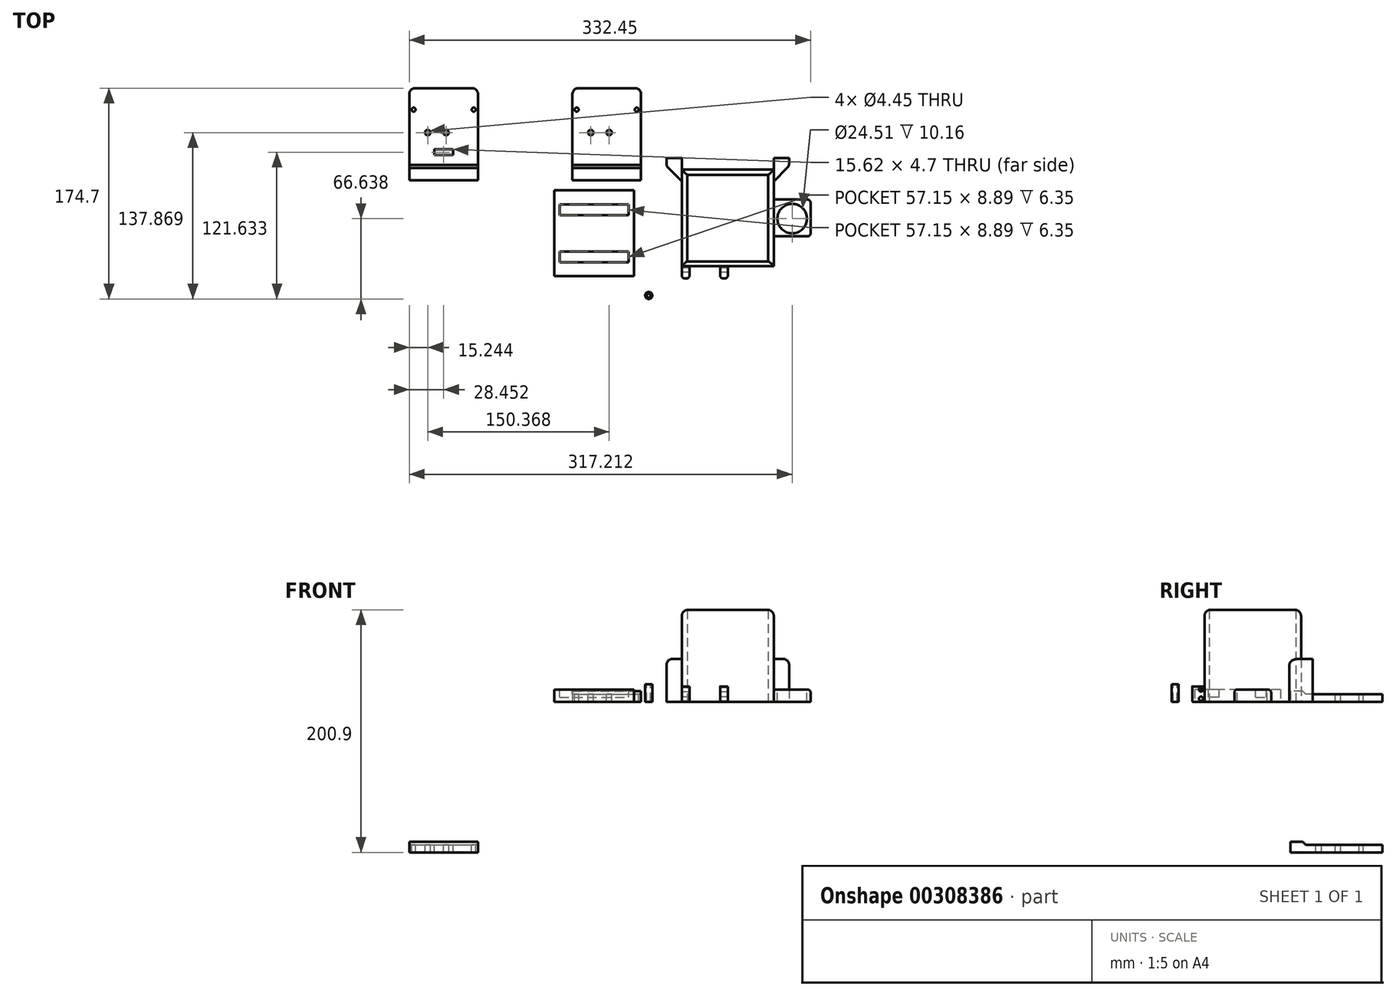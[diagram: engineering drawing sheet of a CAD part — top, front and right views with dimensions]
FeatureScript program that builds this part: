
annotation { "Feature Type Name" : "Feature", "Feature Type Description" : "" }
export const myFeature = defineFeature(function(context is Context, id is Id, definition is map)
    precondition{}
    {
        {
            var Q0;
            Q0=qCreatedBy(makeId("Top.planeOp"),FACE);
            var sketch = newSketch(context, id + "F0", { "sketchPlane" : qUnion([Q0])});
            skLineSegment(sketch, "E0.bottom", {"start": v(-40.77, 32.39) * mm, "end": v(35.43, 32.39) * mm});
            skLineSegment(sketch, "E0.top", {"start": v(-40.77, -43.81) * mm, "end": v(35.43, -43.81) * mm});
            skLineSegment(sketch, "E0.left", {"start": v(-40.77, 32.39) * mm, "end": v(-40.77, -43.81) * mm});
            skLineSegment(sketch, "E0.right", {"start": v(35.43, 32.39) * mm, "end": v(35.43, -43.81) * mm});
            skSolve(sketch);
        }
        {
            var Q0;
            Q0=makeQuery(id+"F0.imprint","IMPRINT",FACE,{"disambiguationData":[TD([[makeQuery(id+"F0.imprint","IMPRINT",EDGE,{"derivedFrom":sQuery(id+"F0.wireOp",EDGE,"E0.bottom")}),-1.0]])]});
            extrude(context, id + "F1", {"entities" : qUnion([Q0]), "depth" : 3.8 * mm});
        }
        {
            var Q0;
            Q0=makeQuery(id+"F1.opExtrude","CAP_FACE",FACE,{"disambiguationData":[OSD([sQuery(id+"F0.wireOp",EDGE,"E0.bottom"),sQuery(id+"F0.wireOp",EDGE,"E0.top"),sQuery(id+"F0.wireOp",EDGE,"E0.left"),sQuery(id+"F0.wireOp",EDGE,"E0.right")])],"isStart":false});
            var sketch = newSketch(context, id + "F2", { "sketchPlane" : qUnion([Q0])});
            skLineSegment(sketch, "E1.bottom", {"start": v(-40.77, -43.81) * mm, "end": v(-34.42, -43.81) * mm});
            skLineSegment(sketch, "E1.top", {"start": v(-40.77, -31.11) * mm, "end": v(-34.42, -31.11) * mm});
            skLineSegment(sketch, "E1.left", {"start": v(-40.77, -43.81) * mm, "end": v(-40.77, -31.11) * mm});
            skLineSegment(sketch, "E1.right", {"start": v(-34.42, -43.81) * mm, "end": v(-34.42, -31.11) * mm});
            skLineSegment(sketch, "E2.bottom", {"start": v(-9.02, -43.81) * mm, "end": v(-2.67, -43.81) * mm});
            skLineSegment(sketch, "E2.top", {"start": v(-9.02, -31.11) * mm, "end": v(-2.67, -31.11) * mm});
            skLineSegment(sketch, "E2.left", {"start": v(-9.02, -43.81) * mm, "end": v(-9.02, -31.11) * mm});
            skLineSegment(sketch, "E2.right", {"start": v(-2.67, -43.81) * mm, "end": v(-2.67, -31.11) * mm});
            skSolve(sketch);
        }
        {
            var Q0;
            Q0 = qSketchRegion(id + "F2", true);
            extrude(context, id + "F3", {"entities" : qUnion([Q0]), "operationType" : NewBodyOperationType.ADD, "depth" : 10.16 * mm});
        }
        {
            var Q0;
            Q0=makeQuery(id+"F3.opExtrude","SWEPT_FACE",FACE,{"disambiguationData":[OSD([sQuery(id+"F2.wireOp",EDGE,"E2.right")])]});
            var sketch = newSketch(context, id + "F4", { "sketchPlane" : qUnion([Q0])});
            skCircle(sketch, "E3", {"center": v(-41.27, 6.65) * mm, "radius": 1.71 * mm});
            skCircle(sketch, "E4", {"center": v(-33.65, 6.65) * mm, "radius": 1.71 * mm});
            skSolve(sketch);
        }
        {
            var Q0;
            Q0 = qSketchRegion(id + "F4", true);
            extrude(context, id + "F5", {"entities" : qUnion([Q0]), "operationType" : NewBodyOperationType.REMOVE, "oppositeDirection" : true, "depth" : 50.8 * mm});
        }
        {
            var Q0;
            Q0=makeQuery(id+"F1.opExtrude","SWEPT_BODY",BODY,{"disambiguationData":[OSD([sQuery(id+"F0.wireOp",EDGE,"E0.bottom"),sQuery(id+"F0.wireOp",EDGE,"E0.top"),sQuery(id+"F0.wireOp",EDGE,"E0.left"),sQuery(id+"F0.wireOp",EDGE,"E0.right")])]});
            var Q1;
            Q1=makeQuery(id+"F1.opExtrude","CAP_EDGE",EDGE,{"disambiguationData":[OSD([sQuery(id+"F0.wireOp",EDGE,"E0.top")])],"isStart":true});
            transform(context, id + "F6", {"entities" : qUnion([Q0]), "transformType" : TransformType.ROTATION, "transformAxis" : qUnion([Q1]), "angle" : 90 * degree, "makeCopy" : false});
        }
        {
            var Q0;
            Q0=makeQuery(id+"F1.opExtrude","CAP_FACE",FACE,{"disambiguationData":[OSD([sQuery(id+"F0.wireOp",EDGE,"E0.bottom"),sQuery(id+"F0.wireOp",EDGE,"E0.top"),sQuery(id+"F0.wireOp",EDGE,"E0.left"),sQuery(id+"F0.wireOp",EDGE,"E0.right")])],"isStart":true});
            var sketch = newSketch(context, id + "F7", { "sketchPlane" : qUnion([Q0])});
            skLineSegment(sketch, "E5.bottom", {"start": v(40.77, 76.2) * mm, "end": v(36.32, 76.2) * mm});
            skLineSegment(sketch, "E5.top", {"start": v(40.77, 0) * mm, "end": v(36.32, 0) * mm});
            skLineSegment(sketch, "E5.left", {"start": v(40.77, 76.2) * mm, "end": v(40.77, 0) * mm});
            skLineSegment(sketch, "E5.right", {"start": v(36.32, 76.2) * mm, "end": v(36.32, 0) * mm});
            skSolve(sketch);
        }
        {
            var Q0;
            Q0=makeQuery(id+"F7.imprint","IMPRINT",FACE,{"disambiguationData":[TD([[makeQuery(id+"F7.imprint","IMPRINT",EDGE,{"derivedFrom":sQuery(id+"F7.wireOp",EDGE,"E5.bottom")}),1.0]])]});
            extrude(context, id + "F8", {"entities" : qUnion([Q0]), "operationType" : NewBodyOperationType.ADD, "depth" : 76.2 * mm});
        }
        {
            var Q0;
            Q0=makeQuery(id+"F8.opExtrude","SWEPT_FACE",FACE,{"disambiguationData":[OSD([sQuery(id+"F7.wireOp",EDGE,"E5.right")])]});
            var sketch = newSketch(context, id + "F9", { "sketchPlane" : qUnion([Q0])});
            skLineSegment(sketch, "E6.bottom", {"start": v(32.39, 76.2) * mm, "end": v(27.94, 76.2) * mm});
            skLineSegment(sketch, "E6.top", {"start": v(32.39, 0) * mm, "end": v(27.94, 0) * mm});
            skLineSegment(sketch, "E6.left", {"start": v(32.39, 76.2) * mm, "end": v(32.39, 0) * mm});
            skLineSegment(sketch, "E6.right", {"start": v(27.94, 76.2) * mm, "end": v(27.94, 0) * mm});
            skSolve(sketch);
        }
        {
            var Q0;
            Q0=makeQuery(id+"F9.imprint","IMPRINT",FACE,{"disambiguationData":[TD([[makeQuery(id+"F9.imprint","IMPRINT",EDGE,{"derivedFrom":sQuery(id+"F9.wireOp",EDGE,"E6.bottom")}),1.0]])]});
            extrude(context, id + "F10", {"entities" : qUnion([Q0]), "operationType" : NewBodyOperationType.ADD, "depth" : 71.75 * mm});
        }
        {
            var Q0;
            Q0=makeQuery(id+"F10.opExtrude","SWEPT_FACE",FACE,{"disambiguationData":[OSD([sQuery(id+"F9.wireOp",EDGE,"E6.right")])]});
            var sketch = newSketch(context, id + "F11", { "sketchPlane" : qUnion([Q0])});
            skLineSegment(sketch, "E7.bottom", {"start": v(35.43, 76.2) * mm, "end": v(30.72, 76.2) * mm});
            skLineSegment(sketch, "E7.top", {"start": v(35.43, 0) * mm, "end": v(30.72, 0) * mm});
            skLineSegment(sketch, "E7.left", {"start": v(35.43, 76.2) * mm, "end": v(35.43, 0) * mm});
            skLineSegment(sketch, "E7.right", {"start": v(30.72, 76.2) * mm, "end": v(30.72, 0) * mm});
            skSolve(sketch);
        }
        {
            var Q0;
            Q0=makeQuery(id+"F11.imprint","IMPRINT",FACE,{"disambiguationData":[TD([[makeQuery(id+"F11.imprint","IMPRINT",EDGE,{"derivedFrom":sQuery(id+"F11.wireOp",EDGE,"E7.bottom")}),1.0]])]});
            extrude(context, id + "F12", {"entities" : qUnion([Q0]), "operationType" : NewBodyOperationType.ADD, "depth" : 73.53 * mm});
        }
        {
            var Q0;
            Q0=makeQuery(id+"F12.boolean.opBoolean","MERGE",FACE,{"derivedFrom":[makeQuery(id+"F10.opExtrude","CAP_FACE",FACE,{"disambiguationData":[OSD([sQuery(id+"F9.wireOp",EDGE,"E6.bottom"),sQuery(id+"F9.wireOp",EDGE,"E6.top"),sQuery(id+"F9.wireOp",EDGE,"E6.left"),sQuery(id+"F9.wireOp",EDGE,"E6.right")])],"isStart":false}),makeQuery(id+"F12.opExtrude","SWEPT_FACE",FACE,{"disambiguationData":[OSD([sQuery(id+"F11.wireOp",EDGE,"E7.left")])]})]});
            var sketch = newSketch(context, id + "F13", { "sketchPlane" : qUnion([Q0])});
            skSolve(sketch);
        }
        {
            var Q0;
            Q0=makeQuery(id+"F8.boolean.opBoolean","MERGE",EDGE,{"derivedFrom":[makeQuery(id+"F1.opExtrude","SWEPT_EDGE",EDGE,{"disambiguationData":[OSD([sQuery(id+"F0.wireOp",EDGE,"E0.bottom"),sQuery(id+"F0.wireOp",EDGE,"E0.left")])]}),makeQuery(id+"F8.opExtrude","SWEPT_EDGE",EDGE,{"disambiguationData":[OSD([sQuery(id+"F7.wireOp",EDGE,"E5.bottom"),sQuery(id+"F7.wireOp",EDGE,"E5.left")])]})]});
            var Q1;
            Q1=makeQuery(id+"F1.opExtrude","CAP_EDGE",EDGE,{"disambiguationData":[OSD([sQuery(id+"F0.wireOp",EDGE,"E0.bottom")])],"isStart":false});
            var Q2;
            Q2=makeQuery(id+"F12.boolean.opBoolean","MERGE",EDGE,{"derivedFrom":[makeQuery(id+"F1.opExtrude","SWEPT_EDGE",EDGE,{"disambiguationData":[OSD([sQuery(id+"F0.wireOp",EDGE,"E0.bottom"),sQuery(id+"F0.wireOp",EDGE,"E0.right")])]}),makeQuery(id+"F10.opExtrude","CAP_EDGE",EDGE,{"disambiguationData":[OSD([sQuery(id+"F9.wireOp",EDGE,"E6.bottom")])],"isStart":false}),makeQuery(id+"F12.opExtrude","SWEPT_EDGE",EDGE,{"disambiguationData":[OSD([sQuery(id+"F11.wireOp",EDGE,"E7.bottom"),sQuery(id+"F11.wireOp",EDGE,"E7.left")])]})]});
            var Q3;
            Q3=makeQuery(id+"F10.boolean.opBoolean","MERGE",EDGE,{"derivedFrom":[makeQuery(id+"F8.opExtrude","CAP_EDGE",EDGE,{"disambiguationData":[OSD([sQuery(id+"F7.wireOp",EDGE,"E5.bottom")])],"isStart":false}),makeQuery(id+"F10.opExtrude","SWEPT_EDGE",EDGE,{"disambiguationData":[OSD([sQuery(id+"F9.wireOp",EDGE,"E6.bottom"),sQuery(id+"F9.wireOp",EDGE,"E6.left")])]})]});
            fillet(context, id + "F14", {"entities" : qUnion([Q0, Q1, Q2, Q3]), "radius" : 5.08 * mm, "tangentPropagation" : true, "allowEdgeOverflow" : false});
        }
        {
            var Q0;
            Q0=makeQuery(id+"F10.boolean.opBoolean","MERGE",FACE,{"derivedFrom":[makeQuery(id+"F8.opExtrude","CAP_FACE",FACE,{"disambiguationData":[OSD([sQuery(id+"F7.wireOp",EDGE,"E5.bottom"),sQuery(id+"F7.wireOp",EDGE,"E5.top"),sQuery(id+"F7.wireOp",EDGE,"E5.left"),sQuery(id+"F7.wireOp",EDGE,"E5.right")])],"isStart":false}),makeQuery(id+"F10.opExtrude","SWEPT_FACE",FACE,{"disambiguationData":[OSD([sQuery(id+"F9.wireOp",EDGE,"E6.left")])]})]});
            var sketch = newSketch(context, id + "F15", { "sketchPlane" : qUnion([Q0])});
            skLineSegment(sketch, "E8.bottom", {"start": v(-35.43, 0) * mm, "end": v(-48.13, 0) * mm});
            skLineSegment(sketch, "E8.top", {"start": v(-35.43, 35.56) * mm, "end": v(-48.13, 35.56) * mm});
            skLineSegment(sketch, "E8.left", {"start": v(-35.43, 0) * mm, "end": v(-35.43, 35.56) * mm});
            skLineSegment(sketch, "E8.right", {"start": v(-48.13, 0) * mm, "end": v(-48.13, 35.56) * mm});
            skLineSegment(sketch, "E9.bottom", {"start": v(40.77, 0) * mm, "end": v(53.47, 0) * mm});
            skLineSegment(sketch, "E9.top", {"start": v(40.77, 35.56) * mm, "end": v(53.47, 35.56) * mm});
            skLineSegment(sketch, "E9.left", {"start": v(40.77, 0) * mm, "end": v(40.77, 35.56) * mm});
            skLineSegment(sketch, "E9.right", {"start": v(53.47, 0) * mm, "end": v(53.47, 35.56) * mm});
            skSolve(sketch);
        }
        {
            var Q0;
            Q0=makeQuery(id+"F15.imprint","IMPRINT",FACE,{"disambiguationData":[TD([[makeQuery(id+"F15.imprint","IMPRINT",EDGE,{"derivedFrom":sQuery(id+"F15.wireOp",EDGE,"E8.bottom")}),-1.0]])]});
            var Q1;
            Q1=makeQuery(id+"F15.imprint","IMPRINT",FACE,{"disambiguationData":[TD([[makeQuery(id+"F15.imprint","IMPRINT",EDGE,{"derivedFrom":sQuery(id+"F15.wireOp",EDGE,"E9.bottom")}),1.0]])]});
            extrude(context, id + "F16", {"entities" : qUnion([Q0, Q1]), "operationType" : NewBodyOperationType.ADD, "endBound" : BoundingType.SYMMETRIC, "depth" : 19.3 * mm});
        }
        {
            var Q0;
            Q0=makeQuery(id+"F16.opExtrude","CAP_EDGE",EDGE,{"disambiguationData":[OSD([sQuery(id+"F15.wireOp",EDGE,"E8.right")])],"isStart":true});
            var Q1;
            Q1=makeQuery(id+"F16.opExtrude","CAP_EDGE",EDGE,{"disambiguationData":[OSD([sQuery(id+"F15.wireOp",EDGE,"E9.right")])],"isStart":true});
            chamfer(context, id + "F17", {"entities" : qUnion([Q0, Q1]), "width" : 12.7 * mm, "tangentPropagation" : true});
        }
        {
            var Q0;
            Q0=makeQuery(id+"F16.opExtrude","SWEPT_EDGE",EDGE,{"disambiguationData":[OSD([sQuery(id+"F15.wireOp",EDGE,"E9.top"),sQuery(id+"F15.wireOp",EDGE,"E9.right")])]});
            var Q1;
            Q1=makeQuery(id+"F16.opExtrude","SWEPT_EDGE",EDGE,{"disambiguationData":[OSD([sQuery(id+"F15.wireOp",EDGE,"E8.top"),sQuery(id+"F15.wireOp",EDGE,"E8.right")])]});
            var Q2;
            Q2=makeQuery(id+"F17.opChamfer","BLEND_EDGE",EDGE,{"blendedFrom":[makeQuery(id+"F16.opExtrude","CAP_EDGE",EDGE,{"disambiguationData":[OSD([sQuery(id+"F15.wireOp",EDGE,"E9.right")])],"isStart":true}),makeQuery(id+"F16.opExtrude","SWEPT_FACE",FACE,{"disambiguationData":[OSD([sQuery(id+"F15.wireOp",EDGE,"E9.top")])]})],"blendedInto":[makeQuery(id+"F16.opExtrude","SWEPT_FACE",FACE,{"disambiguationData":[OSD([sQuery(id+"F15.wireOp",EDGE,"E9.top")])]})]});
            var Q3;
            {var subQ0=sQuery(id+"F15.wireOp",EDGE,"E9.right");Q3=makeQuery(id+"F17.opChamfer","BLEND_EDGE",EDGE,{"blendedFrom":[makeQuery(id+"F16.opExtrude","CAP_EDGE",EDGE,{"disambiguationData":[OSD([subQ0])],"isStart":true}),makeQuery(id+"F16.opExtrude","SWEPT_FACE",FACE,{"disambiguationData":[OSD([subQ0])]})],"blendedInto":[makeQuery(id+"F16.opExtrude","SWEPT_FACE",FACE,{"disambiguationData":[OSD([subQ0])]})]});}
            var Q4;
            Q4=makeQuery(id+"F17.opChamfer","BLEND_EDGE",EDGE,{"blendedFrom":[makeQuery(id+"F16.opExtrude","CAP_EDGE",EDGE,{"disambiguationData":[OSD([sQuery(id+"F15.wireOp",EDGE,"E8.right")])],"isStart":true}),makeQuery(id+"F16.opExtrude","SWEPT_FACE",FACE,{"disambiguationData":[OSD([sQuery(id+"F15.wireOp",EDGE,"E8.top")])]})],"blendedInto":[makeQuery(id+"F16.opExtrude","SWEPT_FACE",FACE,{"disambiguationData":[OSD([sQuery(id+"F15.wireOp",EDGE,"E8.top")])]})]});
            var Q5;
            {var subQ0=sQuery(id+"F15.wireOp",EDGE,"E8.right");Q5=makeQuery(id+"F17.opChamfer","BLEND_EDGE",EDGE,{"blendedFrom":[makeQuery(id+"F16.opExtrude","CAP_EDGE",EDGE,{"disambiguationData":[OSD([subQ0])],"isStart":true}),makeQuery(id+"F16.opExtrude","SWEPT_FACE",FACE,{"disambiguationData":[OSD([subQ0])]})],"blendedInto":[makeQuery(id+"F16.opExtrude","SWEPT_FACE",FACE,{"disambiguationData":[OSD([subQ0])]})]});}
            fillet(context, id + "F18", {"entities" : qUnion([Q0, Q1, Q2, Q3, Q4, Q5]), "radius" : 5.08 * mm, "tangentPropagation" : true, "allowEdgeOverflow" : false});
        }
        {
            var Q0;
            {var subQ0=sQuery(id+"F0.wireOp",EDGE,"E0.right");Q0=makeQuery(id+"F13.imprint","IMPRINT",FACE,{"disambiguationData":[TD([[makeQuery(id+"F13.imprint","IMPRINT",EDGE,{"derivedFrom":makeQuery(id+"F1.opExtrude","CAP_EDGE",EDGE,{"disambiguationData":[OSD([subQ0])],"isStart":false})}),1.0]])]});}
            var sketch = newSketch(context, id + "F19", { "sketchPlane" : qUnion([Q0])});
            skLineSegment(sketch, "E10.bottom", {"start": v(-22.86, 0) * mm, "end": v(7.62, 0) * mm});
            skLineSegment(sketch, "E10.top", {"start": v(-22.86, 10.16) * mm, "end": v(7.62, 10.16) * mm});
            skLineSegment(sketch, "E10.left", {"start": v(-22.86, 0) * mm, "end": v(-22.86, 10.16) * mm});
            skLineSegment(sketch, "E10.right", {"start": v(7.62, 0) * mm, "end": v(7.62, 10.16) * mm});
            skSolve(sketch);
        }
        {
            var Q0;
            Q0 = qSketchRegion(id + "F19", true);
            extrude(context, id + "F20", {"entities" : qUnion([Q0]), "operationType" : NewBodyOperationType.ADD, "depth" : 30.48 * mm});
        }
        {
            var Q0;
            Q0=makeQuery(id+"F20.opExtrude","SWEPT_FACE",FACE,{"disambiguationData":[OSD([sQuery(id+"F19.wireOp",EDGE,"E10.top")])]});
            var sketch = newSketch(context, id + "F21", { "sketchPlane" : qUnion([Q0])});
            skCircle(sketch, "E11", {"center": v(50.67, -8.11) * mm, "radius": 12.26 * mm});
            skSolve(sketch);
        }
        {
            var Q0;
            Q0=makeQuery(id+"F21.imprint","IMPRINT",FACE,{"disambiguationData":[TD([[makeQuery(id+"F21.imprint","IMPRINT",EDGE,{"derivedFrom":sQuery(id+"F21.wireOp",EDGE,"E11")}),1.0]])]});
            extrude(context, id + "F22", {"entities" : qUnion([Q0]), "operationType" : NewBodyOperationType.REMOVE, "oppositeDirection" : true, "depth" : 25.4 * mm});
        }
        {
            var Q0;
            Q0=makeQuery(id+"F20.opExtrude","SWEPT_EDGE",EDGE,{"disambiguationData":[OSD([sQuery(id+"F19.wireOp",EDGE,"E10.top"),sQuery(id+"F19.wireOp",EDGE,"E10.left")])]});
            var Q1;
            Q1=makeQuery(id+"F20.opExtrude","CAP_EDGE",EDGE,{"disambiguationData":[OSD([sQuery(id+"F19.wireOp",EDGE,"E10.top")])],"isStart":false});
            var Q2;
            Q2=makeQuery(id+"F20.opExtrude","SWEPT_EDGE",EDGE,{"disambiguationData":[OSD([sQuery(id+"F19.wireOp",EDGE,"E10.top"),sQuery(id+"F19.wireOp",EDGE,"E10.right")])]});
            var Q3;
            Q3=makeQuery(id+"F20.opExtrude","CAP_EDGE",EDGE,{"disambiguationData":[OSD([sQuery(id+"F19.wireOp",EDGE,"E10.left")])],"isStart":false});
            var Q4;
            Q4=makeQuery(id+"F20.opExtrude","CAP_EDGE",EDGE,{"disambiguationData":[OSD([sQuery(id+"F19.wireOp",EDGE,"E10.right")])],"isStart":false});
            var Q5;
            Q5=makeQuery(id+"F20.opExtrude","CAP_EDGE",EDGE,{"disambiguationData":[OSD([sQuery(id+"F19.wireOp",EDGE,"E10.left")])],"isStart":true});
            fillet(context, id + "F23", {"entities" : qUnion([Q0, Q1, Q2, Q3, Q4, Q5]), "radius" : 2.54 * mm, "tangentPropagation" : true, "allowEdgeOverflow" : false});
        }
        {
            var Q0;
            Q0=makeQuery(id+"F3.opExtrude","CAP_EDGE",EDGE,{"disambiguationData":[OSD([sQuery(id+"F2.wireOp",EDGE,"E2.top")])],"isStart":true});
            var Q1;
            Q1=makeQuery(id+"F3.opExtrude","CAP_EDGE",EDGE,{"disambiguationData":[OSD([sQuery(id+"F2.wireOp",EDGE,"E1.top")])],"isStart":true});
            var Q2;
            Q2=makeQuery(id+"F3.opExtrude","CAP_EDGE",EDGE,{"disambiguationData":[OSD([sQuery(id+"F2.wireOp",EDGE,"E1.right")])],"isStart":false});
            var Q3;
            Q3=makeQuery(id+"F3.opExtrude","CAP_EDGE",EDGE,{"disambiguationData":[OSD([sQuery(id+"F2.wireOp",EDGE,"E1.left")])],"isStart":false});
            var Q4;
            Q4=makeQuery(id+"F3.opExtrude","CAP_EDGE",EDGE,{"disambiguationData":[OSD([sQuery(id+"F2.wireOp",EDGE,"E2.left")])],"isStart":false});
            var Q5;
            Q5=makeQuery(id+"F3.opExtrude","CAP_EDGE",EDGE,{"disambiguationData":[OSD([sQuery(id+"F2.wireOp",EDGE,"E2.right")])],"isStart":false});
            fillet(context, id + "F24", {"entities" : qUnion([Q0, Q1, Q2, Q3, Q4, Q5]), "radius" : 2.54 * mm, "tangentPropagation" : true, "allowEdgeOverflow" : false});
        }
        {
            var Q0;
            Q0=qCreatedBy(makeId("Top.planeOp"),FACE);
            var sketch = newSketch(context, id + "F25", { "sketchPlane" : qUnion([Q0])});
            skLineSegment(sketch, "E12.bottom", {"start": v(-146.35, 15.3) * mm, "end": v(-80.31, 15.3) * mm});
            skLineSegment(sketch, "E12.top", {"start": v(-146.35, -55.82) * mm, "end": v(-80.31, -55.82) * mm});
            skLineSegment(sketch, "E12.left", {"start": v(-146.35, 15.3) * mm, "end": v(-146.35, -55.82) * mm});
            skLineSegment(sketch, "E12.right", {"start": v(-80.31, 15.3) * mm, "end": v(-80.31, -55.82) * mm});
            skSolve(sketch);
        }
        {
            var Q0;
            Q0=makeQuery(id+"F25.imprint","IMPRINT",FACE,{"disambiguationData":[TD([[makeQuery(id+"F25.imprint","IMPRINT",EDGE,{"derivedFrom":sQuery(id+"F25.wireOp",EDGE,"E12.bottom")}),-1.0]])]});
            extrude(context, id + "F26", {"entities" : qUnion([Q0]), "depth" : 10.16 * mm});
        }
        {
            var Q0;
            Q0=makeQuery(id+"F26.opExtrude","CAP_FACE",FACE,{"disambiguationData":[OSD([sQuery(id+"F25.wireOp",EDGE,"E12.bottom"),sQuery(id+"F25.wireOp",EDGE,"E12.top"),sQuery(id+"F25.wireOp",EDGE,"E12.left"),sQuery(id+"F25.wireOp",EDGE,"E12.right")])],"isStart":false});
            var sketch = newSketch(context, id + "F27", { "sketchPlane" : qUnion([Q0])});
            skLineSegment(sketch, "E13.bottom", {"start": v(-141.9, -5.15) * mm, "end": v(-84.76, -5.15) * mm});
            skLineSegment(sketch, "E13.top", {"start": v(-141.9, 3.74) * mm, "end": v(-84.76, 3.74) * mm});
            skLineSegment(sketch, "E13.left", {"start": v(-141.9, -5.15) * mm, "end": v(-141.9, 3.74) * mm});
            skLineSegment(sketch, "E13.right", {"start": v(-84.76, -5.15) * mm, "end": v(-84.76, 3.74) * mm});
            skLineSegment(sketch, "E14.bottom", {"start": v(-141.9, -35.37) * mm, "end": v(-84.76, -35.37) * mm});
            skLineSegment(sketch, "E14.top", {"start": v(-141.9, -44.26) * mm, "end": v(-84.76, -44.26) * mm});
            skLineSegment(sketch, "E14.left", {"start": v(-141.9, -35.37) * mm, "end": v(-141.9, -44.26) * mm});
            skLineSegment(sketch, "E14.right", {"start": v(-84.76, -35.37) * mm, "end": v(-84.76, -44.26) * mm});
            skSolve(sketch);
        }
        {
            var Q0;
            Q0 = qSketchRegion(id + "F27", true);
            extrude(context, id + "F28", {"entities" : qUnion([Q0]), "operationType" : NewBodyOperationType.REMOVE, "oppositeDirection" : true, "depth" : 6.35 * mm});
        }
        {
            var Q0;
            Q0=qCreatedBy(makeId("Top.planeOp"),FACE);
            var sketch = newSketch(context, id + "F29", { "sketchPlane" : qUnion([Q0])});
            skCircle(sketch, "E15", {"center": v(-68.17, -71.83) * mm, "radius": 2.92 * mm});
            skSolve(sketch);
        }
        {
            var Q0;
            Q0=makeQuery(id+"F29.imprint","IMPRINT",FACE,{"disambiguationData":[TD([[makeQuery(id+"F29.imprint","IMPRINT",EDGE,{"derivedFrom":sQuery(id+"F29.wireOp",EDGE,"E15")}),1.0]])]});
            extrude(context, id + "F30", {"entities" : qUnion([Q0]), "depth" : 14.6 * mm});
        }
        {
            var Q0;
            Q0=makeQuery(id+"F30.opExtrude","CAP_FACE",FACE,{"disambiguationData":[OSD([sQuery(id+"F29.wireOp",EDGE,"E15")])],"isStart":false});
            var sketch = newSketch(context, id + "F31", { "sketchPlane" : qUnion([Q0])});
            skCircle(sketch, "E16", {"center": v(-68.17, -71.83) * mm, "radius": 1.59 * mm});
            skSolve(sketch);
        }
        {
            var Q0;
            Q0=makeQuery(id+"F31.imprint","IMPRINT",FACE,{"disambiguationData":[TD([[makeQuery(id+"F31.imprint","IMPRINT",EDGE,{"derivedFrom":sQuery(id+"F31.wireOp",EDGE,"E16")}),1.0]])]});
            extrude(context, id + "F32", {"entities" : qUnion([Q0]), "operationType" : NewBodyOperationType.REMOVE, "oppositeDirection" : true, "depth" : 25.4 * mm});
        }
        {
            var Q0;
            Q0=qCreatedBy(makeId("Top.planeOp"),FACE);
            var sketch = newSketch(context, id + "F33", { "sketchPlane" : qUnion([Q0])});
            skLineSegment(sketch, "E17.bottom", {"start": v(-131.4, 99.95) * mm, "end": v(-74.51, 99.95) * mm});
            skLineSegment(sketch, "E17.top", {"start": v(-131.4, 23.75) * mm, "end": v(-74.51, 23.75) * mm});
            skLineSegment(sketch, "E17.left", {"start": v(-131.4, 99.95) * mm, "end": v(-131.4, 23.75) * mm});
            skLineSegment(sketch, "E17.right", {"start": v(-74.51, 99.95) * mm, "end": v(-74.51, 23.75) * mm});
            skSolve(sketch);
        }
        {
            var Q0;
            Q0=makeQuery(id+"F33.imprint","IMPRINT",FACE,{"disambiguationData":[TD([[makeQuery(id+"F33.imprint","IMPRINT",EDGE,{"derivedFrom":sQuery(id+"F33.wireOp",EDGE,"E17.bottom")}),-1.0]])]});
            extrude(context, id + "F34", {"entities" : qUnion([Q0]), "depth" : 6.35 * mm});
        }
        {
            var Q0;
            Q0=makeQuery(id+"F34.opExtrude","SWEPT_EDGE",EDGE,{"disambiguationData":[OSD([sQuery(id+"F33.wireOp",EDGE,"E17.bottom"),sQuery(id+"F33.wireOp",EDGE,"E17.left")])]});
            var Q1;
            Q1=makeQuery(id+"F34.opExtrude","SWEPT_EDGE",EDGE,{"disambiguationData":[OSD([sQuery(id+"F33.wireOp",EDGE,"E17.bottom"),sQuery(id+"F33.wireOp",EDGE,"E17.right")])]});
            fillet(context, id + "F35", {"entities" : qUnion([Q0, Q1]), "radius" : 5.08 * mm, "tangentPropagation" : true, "allowEdgeOverflow" : false});
        }
        {
            var Q0;
            Q0=makeQuery(id+"F34.opExtrude","CAP_FACE",FACE,{"disambiguationData":[OSD([sQuery(id+"F33.wireOp",EDGE,"E17.bottom"),sQuery(id+"F33.wireOp",EDGE,"E17.top"),sQuery(id+"F33.wireOp",EDGE,"E17.left"),sQuery(id+"F33.wireOp",EDGE,"E17.right")])],"isStart":false});
            var sketch = newSketch(context, id + "F36", { "sketchPlane" : qUnion([Q0])});
            skLineSegment(sketch, "E18.bottom", {"start": v(-131.4, 23.75) * mm, "end": v(-74.51, 23.75) * mm});
            skLineSegment(sketch, "E18.top", {"start": v(-131.4, 36.45) * mm, "end": v(-74.51, 36.45) * mm});
            skLineSegment(sketch, "E18.left", {"start": v(-131.4, 23.75) * mm, "end": v(-131.4, 36.45) * mm});
            skLineSegment(sketch, "E18.right", {"start": v(-74.51, 23.75) * mm, "end": v(-74.51, 36.45) * mm});
            skSolve(sketch);
        }
        {
            var Q0;
            Q0=makeQuery(id+"F36.imprint","IMPRINT",FACE,{"disambiguationData":[TD([[makeQuery(id+"F36.imprint","IMPRINT",EDGE,{"derivedFrom":sQuery(id+"F36.wireOp",EDGE,"E18.bottom")}),1.0]])]});
            extrude(context, id + "F37", {"entities" : qUnion([Q0]), "operationType" : NewBodyOperationType.ADD, "depth" : 2.54 * mm});
        }
        {
            var Q0;
            Q0=makeQuery(id+"F37.opExtrude","CAP_EDGE",EDGE,{"disambiguationData":[OSD([sQuery(id+"F36.wireOp",EDGE,"E18.top")])],"isStart":false});
            chamfer(context, id + "F38", {"entities" : qUnion([Q0]), "width" : 2.54 * mm, "tangentPropagation" : true});
        }
        {
            var Q0;
            Q0=makeQuery(id+"F34.opExtrude","CAP_FACE",FACE,{"disambiguationData":[OSD([sQuery(id+"F33.wireOp",EDGE,"E17.bottom"),sQuery(id+"F33.wireOp",EDGE,"E17.top"),sQuery(id+"F33.wireOp",EDGE,"E17.left"),sQuery(id+"F33.wireOp",EDGE,"E17.right")])],"isStart":false});
            var sketch = newSketch(context, id + "F39", { "sketchPlane" : qUnion([Q0])});
            skCircle(sketch, "E19", {"center": v(-78.07, 82.17) * mm, "radius": 1.65 * mm});
            skCircle(sketch, "E20", {"center": v(-127.85, 82.17) * mm, "radius": 1.65 * mm});
            skCircle(sketch, "E21", {"center": v(-100.93, 63.12) * mm, "radius": 2.22 * mm});
            skCircle(sketch, "E22", {"center": v(-116.17, 63.12) * mm, "radius": 2.22 * mm});
            skSolve(sketch);
        }
        {
            var Q0;
            Q0 = qSketchRegion(id + "F39", true);
            extrude(context, id + "F40", {"entities" : qUnion([Q0]), "operationType" : NewBodyOperationType.REMOVE, "oppositeDirection" : true, "depth" : 25.4 * mm});
        }
        {
            var Q0;
            Q0=makeQuery(id+"F34.opExtrude","SWEPT_BODY",BODY,{"disambiguationData":[OSD([sQuery(id+"F33.wireOp",EDGE,"E17.bottom"),sQuery(id+"F33.wireOp",EDGE,"E17.top"),sQuery(id+"F33.wireOp",EDGE,"E17.left"),sQuery(id+"F33.wireOp",EDGE,"E17.right")])]});
            transform(context, id + "F41", {"entities" : qUnion([Q0]), "transformType" : TransformType.TRANSLATION_3D, "dx" : -135.13 * mm, "dy" : 0 * mm, "dz" : -124.7 * mm, "makeCopy" : true});
        }
        {
            var Q0;
            Q0=makeQuery(id+"F41.opPattern","COPY",FACE,{"derivedFrom":makeQuery(id+"F34.opExtrude","CAP_FACE",FACE,{"disambiguationData":[OSD([sQuery(id+"F33.wireOp",EDGE,"E17.bottom"),sQuery(id+"F33.wireOp",EDGE,"E17.top"),sQuery(id+"F33.wireOp",EDGE,"E17.left"),sQuery(id+"F33.wireOp",EDGE,"E17.right")])],"isStart":false}),"instanceName":"1"});
            var sketch = newSketch(context, id + "F42", { "sketchPlane" : qUnion([Q0])});
            skLineSegment(sketch, "E23.bottom", {"start": v(-245.9, 49.23) * mm, "end": v(-230.28, 49.23) * mm});
            skLineSegment(sketch, "E23.top", {"start": v(-245.9, 44.53) * mm, "end": v(-230.28, 44.53) * mm});
            skLineSegment(sketch, "E23.left", {"start": v(-245.9, 49.23) * mm, "end": v(-245.9, 44.53) * mm});
            skLineSegment(sketch, "E23.right", {"start": v(-230.28, 49.23) * mm, "end": v(-230.28, 44.53) * mm});
            skSolve(sketch);
        }
        {
            var Q0;
            Q0=makeQuery(id+"F42.imprint","IMPRINT",FACE,{"disambiguationData":[TD([[makeQuery(id+"F42.imprint","IMPRINT",EDGE,{"derivedFrom":sQuery(id+"F42.wireOp",EDGE,"E23.bottom")}),-1.0]])]});
            extrude(context, id + "F43", {"entities" : qUnion([Q0]), "operationType" : NewBodyOperationType.REMOVE, "oppositeDirection" : true, "depth" : 25.4 * mm});
        }
    });
